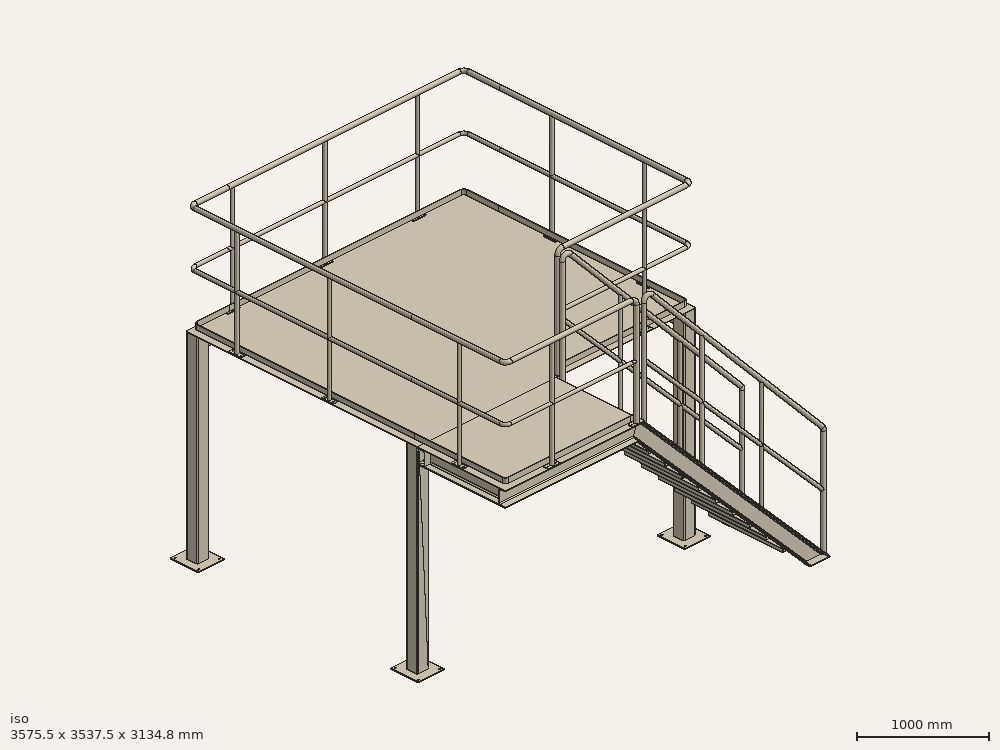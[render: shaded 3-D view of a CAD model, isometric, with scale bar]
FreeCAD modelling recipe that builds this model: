
FCSTD DOCUMENT  (FreeCAD 1.0R39319 (Git))
Label: trestle011
License: All rights reserved
objects: Part::FeaturePython×11, Sketcher::SketchObject×2, App::Part×2, Spreadsheet::Sheet×1, Part::Extrusion×1, PartDesign::Pad×1
note: 19 computed .brp shape members not serialized (recipe doc carries the construction recipe); baked Part::Feature solids carry a one-line shape summary decoded from their .brp

FEATURE [Spreadsheet::Sheet] Spreadsheet
  cells = A1(key)='01; A2='W; B2(W0)=3000; A3='L; B3(L0)=2500; A4='H; B4(H0)=2000
FEATURE [Sketcher::SketchObject] Sketch
  ArcFitTolerance = 0
  FullyConstrained = true
  MakeInternals = false
  expr: Constraints[8] = Spreadsheet.L0
  expr: Constraints[9] = Spreadsheet.W0
  sketch-geometry (4):
    g0: LineSegment StartX=-62.5 StartY=-62.5 StartZ=0 EndX=2937.5 EndY=-62.5 EndZ=0
    g1: LineSegment StartX=2937.5 StartY=-62.5 StartZ=0 EndX=2937.5 EndY=2437.5 EndZ=0
    g2: LineSegment StartX=2937.5 StartY=2437.5 StartZ=0 EndX=-62.5 EndY=2437.5 EndZ=0
    g3: LineSegment StartX=-62.5 StartY=2437.5 StartZ=0 EndX=-62.5 EndY=-62.5 EndZ=0
  constraints (12):
    c: Coincident(g0,g1)
    c: Coincident(g1,g2)
    c: Coincident(g2,g3)
    c: Coincident(g3,g0)
    c: Horizontal(g0)
    c: Horizontal(g2)
    c: Vertical(g1)
    c: Vertical(g3)
    c: DistanceY(g3,g3) = 2500
    c: DistanceX(g2,g2) = 3000
    c: DistanceY(g0,g-1) = 62.5
    c: DistanceX(g0,g-1) = 62.5
FEATURE [Part::Extrusion] Extrude001  label="chpl"
  Base = -> Sketch
  Dir = (0,0,1)
  DirMode = 2
  FaceMakerClass = Part::FaceMakerBullseye
  FaceMakerMode = 3
  LengthFwd = 4.5
  LengthRev = 0
  Placement = pos=(0,0,2000) rot=(0,0,1;0rad)
  Solid = true
  Symmetric = false
  expr: .Placement.Base.z = Spreadsheet.H0
FEATURE [Part::FeaturePython] stair  # WARN: FeaturePython — macro-defined, semantics opaque (R4)
  ClockWise = true
  H = 2000
  L = 2000
  L1 = 1500
  MdlFloor = false
  Placement = pos=(3437.5,-937.5,0) rot=(0,0,1;3.14159rad)
  Rail = 0
  Standard = L=2000.0
  body = 284.113
  handrail = 54.2281
  mass = 338.342
  size = 1
  story = 2
  t = 9
  t0 = 0
  type = 1
  w0 = 800
  w1 = 950
  w2 = 0
  w3 = 0
  expr: .Placement.Base.x = Spreadsheet.H0 + 1500 - 62.5
FEATURE [Part::FeaturePython] Corner_with_end  # WARN: FeaturePython — macro-defined, semantics opaque (R4)
  Placement = pos=(1373,-987,2004.5) rot=(0,0,1;3.14159rad)
  Reverse = true
  Standard = L1=1410.0,L2=1000.0
  g0 = 7.85
  h = 1100
  k = -90
  l1 = 1410
  l2 = 1000
  mass = 29.375
  p = 1000
  spec = 0
  type = 1
  expr: .Placement.Base.z = Spreadsheet.H0 + 4.5
FEATURE [Part::FeaturePython] Corner  # WARN: FeaturePython — macro-defined, semantics opaque (R4)
  Placement = pos=(-37,13,2004.5) rot=(0,0,1;1.5708rad)
  Reverse = true
  Standard = L1=2400.0,L2=400.0
  g0 = 7.85
  h = 1100
  k = -90
  l1 = 2400
  l2 = 400
  mass = 28.4497
  p = 1000
  spec = 0
  type = 2
  expr: .Placement.Base.z = Spreadsheet.H0 + 4.5
  expr: l1 = Spreadsheet.L0 - 100
FEATURE [Part::FeaturePython] Corner001  # WARN: FeaturePython — macro-defined, semantics opaque (R4)
  Placement = pos=(363,2413,2004.5) rot=(0,0,1;0rad)
  Reverse = true
  Standard = L1=2550.0,L2=400.0
  g0 = 7.85
  h = 1100
  k = -90
  l1 = 2550
  l2 = 400
  mass = 32.5879
  p = 1000
  spec = 0
  type = 2
  expr: .Placement.Base.y = Spreadsheet.L0 - 87
  expr: .Placement.Base.z = Spreadsheet.H0 + 4.5
  expr: l1 = Spreadsheet.W0 - 450
FEATURE [Part::FeaturePython] Corner_with_end001  # WARN: FeaturePython — macro-defined, semantics opaque (R4)
  Placement = pos=(1473,-37,2004.5) rot=(0,0,1;0rad)
  Reverse = false
  Standard = L1=1440.0,L2=2050.0
  g0 = 7.85
  h = 1100
  k = 90
  l1 = 1440
  l2 = 2050
  mass = 41.1116
  p = 1000
  spec = 0
  type = 1
  expr: .Placement.Base.z = Spreadsheet.H0 + 4.5
  expr: l1 = Spreadsheet.W0 - 1560
  expr: l2 = Spreadsheet.L0 - 450
FEATURE [Sketcher::SketchObject] Sketch001
  ArcFitTolerance = 1e-06
  FullyConstrained = true
  MakeInternals = false
  MapMode = 5
  Placement = pos=(0,0,0) rot=(1,0,0;3.14159rad)
  sketch-geometry (9):
    g0: LineSegment StartX=-138 StartY=-150 StartZ=0 EndX=138 EndY=-150 EndZ=0
    g1: LineSegment StartX=138 StartY=-150 StartZ=0 EndX=138 EndY=150 EndZ=0
    g2: LineSegment StartX=138 StartY=150 StartZ=0 EndX=-138 EndY=150 EndZ=0
    g3: LineSegment StartX=-138 StartY=150 StartZ=0 EndX=-138 EndY=-150 EndZ=0
    g4: GeomPoint [constr] X=-2e-16 Y=3e-16 Z=0
    g5: Circle CenterX=-113 CenterY=125 CenterZ=0 NormalX=0 NormalY=0 NormalZ=1 AngleXU=0 Radius=10
    g6: Circle CenterX=-113 CenterY=-125 CenterZ=0 NormalX=0 NormalY=0 NormalZ=1 AngleXU=0 Radius=10
    g7: Circle CenterX=113 CenterY=-125 CenterZ=0 NormalX=0 NormalY=0 NormalZ=1 AngleXU=0 Radius=10
    g8: Circle CenterX=113 CenterY=125 CenterZ=0 NormalX=0 NormalY=0 NormalZ=1 AngleXU=0 Radius=10
  constraints (24):
    c: Coincident(g0,g1)
    c: Coincident(g1,g2)
    c: Coincident(g2,g3)
    c: Coincident(g3,g0)
    c: Horizontal(g0)
    c: Horizontal(g2)
    c: Vertical(g1)
    c: Vertical(g3)
    c: Symmetric(g2,g0,g4)
    c: Coincident(g4,g-1)
    c: DistanceY(g-3,g1) = 50
    c: DistanceX(g-5,g0) = 50
    c: Diameter(g5) = 20
    c: Equal(g5,g6)
    c: Equal(g6,g7)
    c: Equal(g7,g8)
    c: Vertical(g5,g6)
    c: Vertical(g8,g7)
    c: Horizontal(g5,g8)
    c: Horizontal(g6,g7)
    c: DistanceY(g5,g2) = 25
    c: DistanceX(g2,g5) = 25
    c: DistanceX(g8,g1) = 25
    c: DistanceY(g0,g7) = 25
FEATURE [PartDesign::Pad] Pad  label="plt"
  Direction = (0,-1e-16,-1)
  Length = 9
  Length2 = 10
  Placement = pos=(0,0,0) rot=(1,0,0;3.14159rad)
  Profile = -> Sketch001
  ReferenceAxis = -> Sketch001 [N_Axis]
  Refine = true
  Suppressed = false
  Type = 0
FEATURE [Part::FeaturePython] SquarePipe  # WARN: FeaturePython — macro-defined, semantics opaque (R4)
  A = 125
  B = 125
  JPN = 角形鋼管
  L = 2000
  Placement = pos=(0,0,0) rot=(1,0,0;1.5708rad)
  Solid = true
  Standard = L=2200
  g0 = 7.85
  mass = 43.3837
  size = 40
  standard = SS
  t = 6
  type = 10_Square_Pipe
  expr: L = Spreadsheet.H0
FEATURE [App::Part] Part001  label="pst_SQ"
  Group = -> [Pad,Sketch001,SquarePipe]
  JPN = 支柱
  Origin = -> Origin001
  Standard = □125x125x6 , H=2200
  count = 1
  g0 = 7.85
  mass = 84.5691
  material = SS41
FEATURE [Part::FeaturePython] Array  # Draft array (typed FeaturePython)
  Angle = 360
  ArrayType = 0
  Axis = (0,0,1)
  Base = -> Part001
  Center = (0,0,0)
  Count = 4
  Fuse = true
  IntervalAxis = (0,0,0)
  IntervalX = (2875,0,0)
  IntervalY = (0,2375,0)
  IntervalZ = (0,0,100)
  NumberCircles = 3
  NumberPolar = 5
  NumberX = 2
  NumberY = 2
  NumberZ = 1
  RadialDistance = 50
  Symmetry = 1
  TangentialDistance = 25
  expr: .IntervalX.x = Spreadsheet.W0 - 125
  expr: .IntervalY.y = Spreadsheet.L0 - 125
FEATURE [Part::FeaturePython] ChannelSteel  # WARN: FeaturePython — macro-defined, semantics opaque (R4)
  B = 75
  H = 150
  JPN = 溝形鋼
  L = 2250
  Placement = pos=(0,67.5,1925) rot=(0,1,0;3.14159rad)
  Solid = true
  Standard = L=2250
  g0 = 7.85
  mass = 33.8098
  size = 3
  standard = SS
  t1 = 6.5
  t2 = 10
  type = 01_Channel
  expr: .Placement.Base.z = Spreadsheet.H0 - 75
  expr: L = Spreadsheet.L0 - 250
FEATURE [Part::FeaturePython] Clone  label="ChannelSteel001"  # Draft clone (typed FeaturePython)
  AttacherType = Attacher::AttachEngine3D
  Fuse = false
  Objects = -> [ChannelSteel]
  Placement = pos=(2875,67.5,1925) rot=(0,0,1;0rad)
  Scale = (1,1,1)
  expr: .Placement.Base.x = Spreadsheet.W0 - 125
  expr: .Placement.Base.z = Spreadsheet.H0 - 75
FEATURE [Part::FeaturePython] ChannelSteel001  label="ChannelSteel002"  # WARN: FeaturePython — macro-defined, semantics opaque (R4)
  B = 75
  H = 150
  JPN = 溝形鋼
  L = 2750
  Placement = pos=(62.5,0,1925) rot=(0,0,1;4.71239rad)
  Solid = true
  Standard = L=2750
  g0 = 7.85
  mass = 92.9768
  size = 3
  standard = SS
  t1 = 6.5
  t2 = 10
  type = 01_Channel
  expr: .Placement.Base.z = Spreadsheet.H0 - 75
  expr: L = Spreadsheet.W0 - 250
FEATURE [Part::FeaturePython] Clone001  label="ChannelSteel003"  # Draft clone (typed FeaturePython)
  AttacherType = Attacher::AttachEngine3D
  Fuse = false
  Objects = -> [ChannelSteel001]
  Placement = pos=(62.5,2375,1925) rot=(-0.707107,-0.707107,0;3.14159rad)
  Scale = (1,1,1)
  expr: .Placement.Base.y = Spreadsheet.L0 - 125
  expr: .Placement.Base.z = Spreadsheet.H0 - 75
FEATURE [App::Part] Part  label="Trstle01"
  Group = -> [Spreadsheet,Sketch,Extrude001,stair,Corner_with_end,Corner,Corner001,Corner_with_end001,Part001,Array,ChannelSteel,Clone,ChannelSteel001,Clone001]
  Origin = -> Origin
